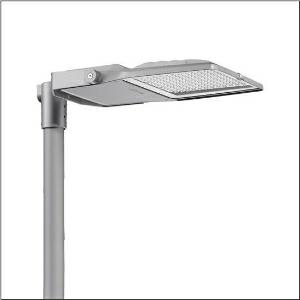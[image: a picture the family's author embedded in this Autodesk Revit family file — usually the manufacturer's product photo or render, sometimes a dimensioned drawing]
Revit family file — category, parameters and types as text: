
# Revit family: floodlight_fl_21_midi___pl43_5xa7786e2a3a_b253
name_source: partatom
category: Lighting Fixtures
units: mm (PartAtom-declared; Revit-internal decimal feet)

## family parameters
Cut with Voids When Loaded = No
Host = Face
Light Source = No
Part Type = Normal
Room Calculation Point = No
Round Connector Dimension = Use Diameter
Shared = No

## types (1)
- --- (1 x LED, 27640 lm, 212.4 W, 3000K)
    Apparent Load = 212 VA
    CIE Flux Codes = 27 78 99 100 100
    Color Rendering = 70
    Color Temperature = 3000K
    Default Elevation = 1800 mm
    Description = Floodlight FL 21 midi, floodlight, primary light control with lens, of PMMA, primary optical cover: protective disc, of toughened safety glass, transparent, light distribution: PL43, light emission: direct distribution, installation type: surface-mounted, LED, High Power LED, rated luminous flux: 27.640lm, luminous efficacy: 130lm/W, light colour: 730, colour temperature: 3000K, control gear: Smart Interface (Zhaga), control: flexible luminous flux parameterisation, time-dependent luminous flux control, constant luminous flux control, overheat protection, pre-setting: logarithmic dimming characteristic, with terminal, 6-pole, mains connection: 220..240V, AC, 50/60Hz, start of lifetime: 212W, end of service life: 231W, reduction: 95W, luminaire housing, of diecast aluminium, powder-coated, Siteco® metallic grey (DB 702S), corrosivity category C5 mid according to DIN EN ISO 12944, suitable for swimming pools, chlorine-resistant, sealing non-destructively replaceable, please order mast flange separately, mast bracket, of steel, galvanised, powder-coated, Siteco® metallic grey (DB 702S), Smart Interface below and above, protection rating (complete): IP66, insulation class (complete): insulation class II (safety insulation), certification: CE, ENEC, VDE, protection symbol: D, impact resistance: IK08, permissible operating ambient temperature: -40..+40°C, permissible operating ambient temperature for outdoor applications: -40..+50°C, standard: DIN EN 12944, LABS conformity tested according to VDMA 24364:2018-05, packaging unit: 1 piece

Light Distribution: PL43
    Height = 76 mm
    Lamp = 1 x LED
    Lamp Light Flux = 27640 lm
    Lamp Power = 212.4 W
    Lamp count = 1
    Length = 657 mm
    Luminous efficacy = 130 lm/W
    Manufacturer = Siteco
    ModVariant = No
    Model = 5XA7786E2A3A
    Number of Poles = 1
    OnlyDefault = Yes
    Power Factor = 1
    Product Name = Floodlight FL 21 midi | PL43
    Product group = floodlight | pylon annexe
    ProductGroupID = 6200
    Protection Class = Protection class II
    Protection Degree = IP 66
    RLX_Detail_Level = 1
    RLX_Emergency_Light_Flux = 0 lm
    RLX_Emergency_Type = 0
    RLX_Emergency_Type_DB = No
    RlxData = <blob elided: 153417 chars, md5=40396740>
    Socket = socket
    Standby Power = 0 W
    System Light Flux = 27640 lm
    System Power = 212 W
    Type Comments = factory setting: luminous flux: 100 % | dim-lin: 254 | 710 mA
    Type Image = l_1007123.jpg
    URL = http://relux.com
    VarID = @adj_177250
    Voltage = 0 V
    Weight = 0.00 kg
    Width = 442 mm

## geometry (parser evidence)
native form markers: Blend x4, Sweep x12
no freeform markers — native parametric forms only
